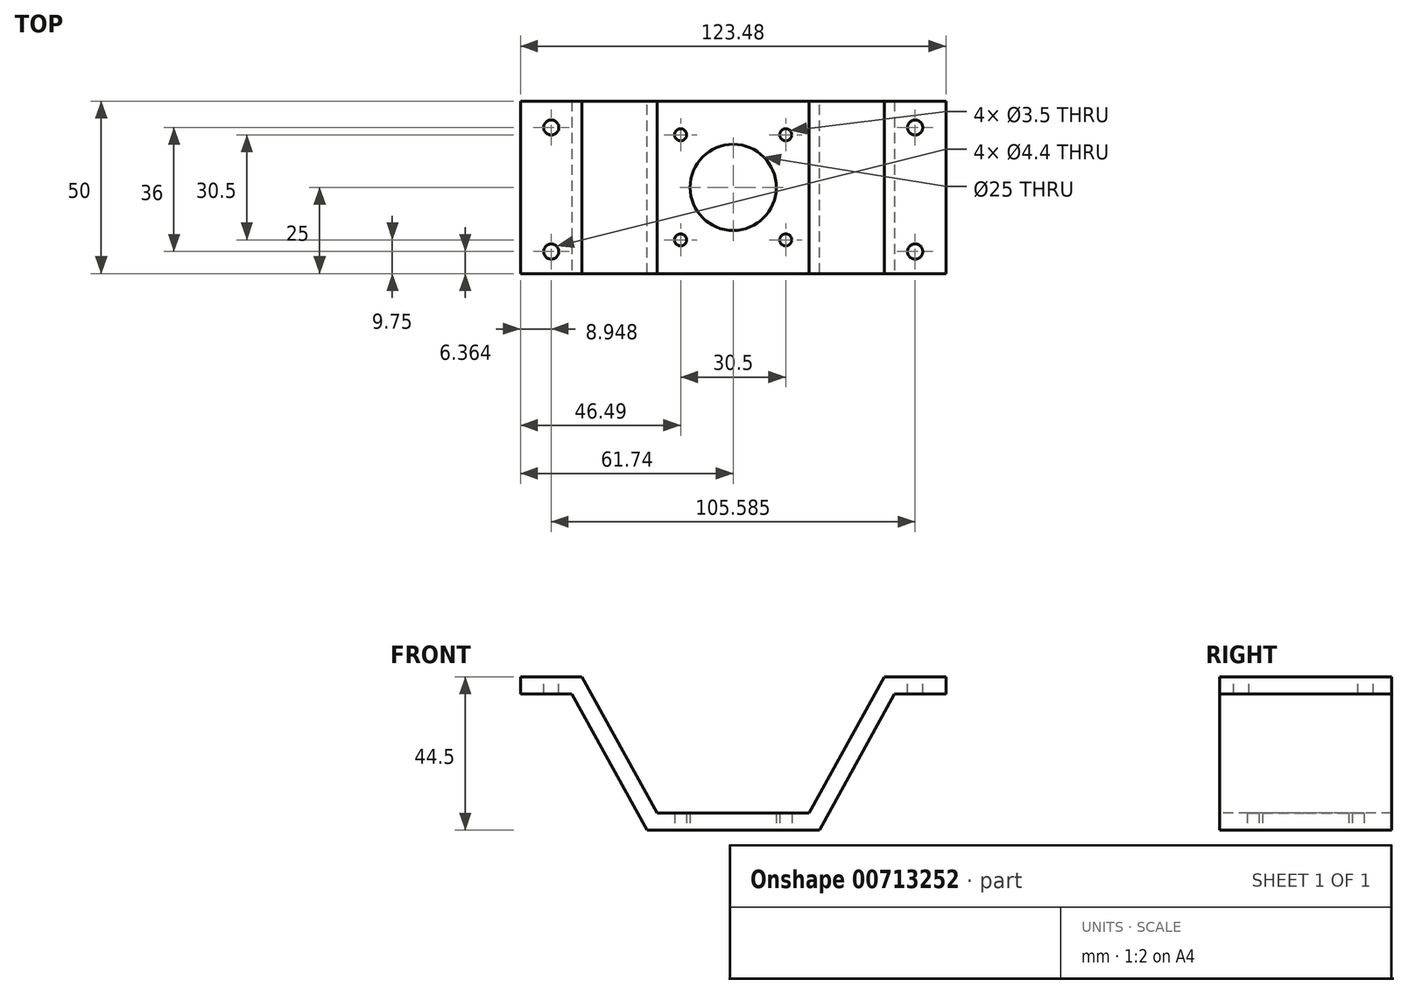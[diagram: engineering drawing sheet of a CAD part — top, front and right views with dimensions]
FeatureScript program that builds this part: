
annotation { "Feature Type Name" : "Feature", "Feature Type Description" : "" }
export const myFeature = defineFeature(function(context is Context, id is Id, definition is map)
    precondition{}
    {
        {
            var Q0;
            Q0=qCreatedBy(makeId("Top.planeOp"),FACE);
            var sketch = newSketch(context, id + "F0", { "sketchPlane" : qUnion([Q0])});
            skPoint(sketch, "E0.middle", {"position": v(0, 0) * mm});
            skCircle(sketch, "E1", {"center": v(-15.25, 15.25) * mm, "radius": 1.75 * mm});
            skCircle(sketch, "E2", {"center": v(15.25, 15.25) * mm, "radius": 1.75 * mm});
            skCircle(sketch, "E3", {"center": v(-15.25, -15.25) * mm, "radius": 1.75 * mm});
            skCircle(sketch, "E4", {"center": v(15.25, -15.25) * mm, "radius": 1.75 * mm});
            skLineSegment(sketch, "E5.bottom", {"start": v(25, -25) * mm, "end": v(-25, -25) * mm});
            skLineSegment(sketch, "E5.top", {"start": v(25, 25) * mm, "end": v(-25, 25) * mm});
            skLineSegment(sketch, "E5.left", {"start": v(25, -25) * mm, "end": v(25, 25) * mm});
            skLineSegment(sketch, "E5.right", {"start": v(-25, -25) * mm, "end": v(-25, 25) * mm});
            skCircle(sketch, "E6", {"center": v(0, 0) * mm, "radius": 12.5 * mm});
            skSolve(sketch);
        }
        {
            var Q0;
            Q0=makeQuery(id+"F0.imprint","IMPRINT",FACE,{"disambiguationData":[TD([[makeQuery(id+"F0.imprint","IMPRINT",EDGE,{"derivedFrom":sQuery(id+"F0.wireOp",EDGE,"E1")}),-1.0]])]});
            extrude(context, id + "F1", {"entities" : qUnion([Q0]), "depth" : 5 * mm, "offsetDistance" : 25 * mm});
        }
        {
            var Q0;
            Q0=makeQuery(id+"F1.opExtrude","SWEPT_FACE",FACE,{"disambiguationData":[OSD([sQuery(id+"F0.wireOp",EDGE,"E5.bottom")])]});
            var sketch = newSketch(context, id + "F2", { "sketchPlane" : qUnion([Q0])});
            skLineSegment(sketch, "E7", {"start": v(25, 0) * mm, "end": v(46.8, 39.5) * mm});
            skLineSegment(sketch, "E8", {"start": v(46.8, 39.5) * mm, "end": v(61.74, 39.5) * mm});
            skLineSegment(sketch, "E9", {"start": v(61.74, 39.5) * mm, "end": v(61.74, 44.5) * mm});
            skLineSegment(sketch, "E10", {"start": v(61.74, 44.5) * mm, "end": v(43.85, 44.5) * mm});
            skLineSegment(sketch, "E11", {"start": v(43.85, 44.5) * mm, "end": v(22.05, 5) * mm});
            skLineSegment(sketch, "E12", {"start": v(22.05, 5) * mm, "end": v(25, 5) * mm});
            skLineSegment(sketch, "E13", {"start": v(25, 5) * mm, "end": v(25, 0) * mm});
            skLineSegment(sketch, "E14.MirrorCS", {"start": v(-25, 5) * mm, "end": v(-25, 0) * mm});
            skLineSegment(sketch, "E15.MirrorCS", {"start": v(-22.05, 5) * mm, "end": v(-25, 5) * mm});
            skLineSegment(sketch, "E16.MirrorCS", {"start": v(-61.74, 39.5) * mm, "end": v(-61.74, 44.5) * mm});
            skLineSegment(sketch, "E17.MirrorCS", {"start": v(-43.85, 44.5) * mm, "end": v(-22.05, 5) * mm});
            skLineSegment(sketch, "E18.MirrorCS", {"start": v(-61.74, 44.5) * mm, "end": v(-43.85, 44.5) * mm});
            skLineSegment(sketch, "E19.MirrorCS", {"start": v(-25, 0) * mm, "end": v(-46.8, 39.5) * mm});
            skLineSegment(sketch, "E20.MirrorCS", {"start": v(-46.8, 39.5) * mm, "end": v(-61.74, 39.5) * mm});
            skSolve(sketch);
        }
        {
            var Q0;
            Q0=makeQuery(id+"F2.imprint","IMPRINT",FACE,{"disambiguationData":[TD([[makeQuery(id+"F2.imprint","IMPRINT",EDGE,{"derivedFrom":sQuery(id+"F2.wireOp",EDGE,"E14.MirrorCS")}),-1.0]])]});
            var Q1;
            Q1=makeQuery(id+"F2.imprint","IMPRINT",FACE,{"disambiguationData":[TD([[makeQuery(id+"F2.imprint","IMPRINT",EDGE,{"derivedFrom":sQuery(id+"F2.wireOp",EDGE,"E7")}),1.0]])]});
            var Q2;
            Q2=makeQuery(id+"F1.opExtrude","CAP_VERTEX",VERTEX,{"disambiguationData":[OSD([sQuery(id+"F0.wireOp",EDGE,"E5.top"),sQuery(id+"F0.wireOp",EDGE,"E5.right")])],"isStart":false});
            extrude(context, id + "F3", {"entities" : qUnion([Q0, Q1]), "operationType" : NewBodyOperationType.ADD, "endBound" : BoundingType.UP_TO_VERTEX, "oppositeDirection" : true, "depth" : 25 * mm, "endBoundEntityVertex" : qUnion([Q2]), "offsetDistance" : 25 * mm});
        }
        {
            var Q0;
            Q0=makeQuery(id+"F3.opExtrude","SWEPT_FACE",FACE,{"disambiguationData":[OSD([sQuery(id+"F2.wireOp",EDGE,"E10")])]});
            var sketch = newSketch(context, id + "F4", { "sketchPlane" : qUnion([Q0])});
            skLineSegment(sketch, "E21.bottom", {"start": v(-52.8, 17.36) * mm, "end": v(52.8, 17.36) * mm});
            skLineSegment(sketch, "E21.top", {"start": v(-52.8, -18.64) * mm, "end": v(52.8, -18.64) * mm});
            skLineSegment(sketch, "E21.left", {"start": v(-52.8, 17.36) * mm, "end": v(-52.8, -18.64) * mm});
            skLineSegment(sketch, "E21.right", {"start": v(52.8, 17.36) * mm, "end": v(52.8, -18.64) * mm});
            skSolve(sketch);
        }
        {
            var Q0;
            Q0=sQuery(id+"F4.wireOp",VERTEX,"E21.bottom.start");
            var Q1;
            Q1=sQuery(id+"F4.wireOp",VERTEX,"E21.top.start");
            var Q2;
            Q2=sQuery(id+"F4.wireOp",VERTEX,"E21.right.end");
            var Q3;
            Q3=sQuery(id+"F4.wireOp",VERTEX,"E21.bottom.end");
            var Q4;
            Q4=makeQuery(id+"F1.opExtrude","SWEPT_BODY",BODY,{"disambiguationData":[OSD([sQuery(id+"F0.wireOp",EDGE,"E1"),sQuery(id+"F0.wireOp",EDGE,"E2"),sQuery(id+"F0.wireOp",EDGE,"E3"),sQuery(id+"F0.wireOp",EDGE,"E4"),sQuery(id+"F0.wireOp",EDGE,"E5.bottom"),sQuery(id+"F0.wireOp",EDGE,"E5.top"),sQuery(id+"F0.wireOp",EDGE,"E5.left"),sQuery(id+"F0.wireOp",EDGE,"E5.right"),sQuery(id+"F0.wireOp",EDGE,"E6")])]});
            hole(context, id + "F5", {"style" : HoleStyle.SIMPLE, "endStyle" : HoleEndStyle.THROUGH, "standardTappedOrClearance" : lookupTablePath({ "standard" : "ISO", "fit" : "Normal", "size" : "M4", "type" : "Clearance" }), "standardBlindInLast" : lookupTablePath({ "fit" : "Standard", "standard" : "ISO", "size" : "M4", "type" : "Clearance" }), "holeDiameter" : 4.4 * mm, "majorDiameter" : 5 * mm, "isTappedThrough" : true, "tappedDepth" : 12 * mm, "tapClearance" : 3, "startFromSketch" : true, "locations" : qUnion([Q0, Q1, Q2, Q3]), "scope" : qUnion([Q4])});
        }
    });
